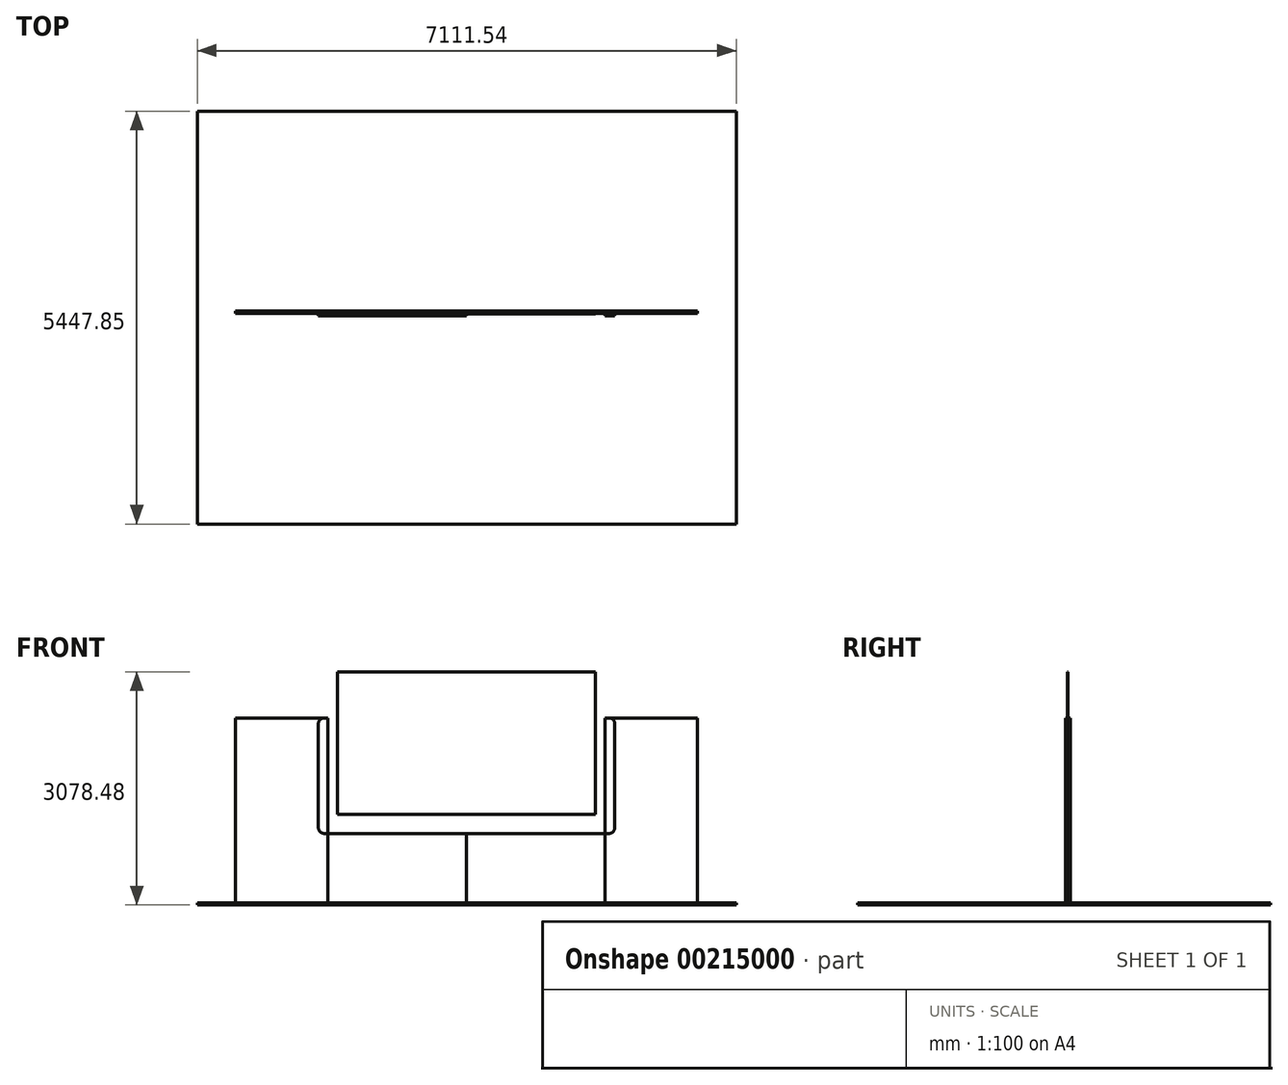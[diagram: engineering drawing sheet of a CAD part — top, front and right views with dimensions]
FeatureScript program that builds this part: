
annotation { "Feature Type Name" : "Feature", "Feature Type Description" : "" }
export const myFeature = defineFeature(function(context is Context, id is Id, definition is map)
    precondition{}
    {
        {
            var Q0;
            Q0=qCreatedBy(makeId("Front.planeOp"),FACE);
            var sketch = newSketch(context, id + "F0", { "sketchPlane" : qUnion([Q0])});
            skLineSegment(sketch, "E0.bottom", {"start": v(0, 0) * mm, "end": v(1219.2, 0) * mm});
            skLineSegment(sketch, "E0.top", {"start": v(0, 2438.4) * mm, "end": v(1219.2, 2438.4) * mm});
            skLineSegment(sketch, "E0.left", {"start": v(0, 0) * mm, "end": v(0, 2438.4) * mm});
            skLineSegment(sketch, "E0.right", {"start": v(1219.2, 0) * mm, "end": v(1219.2, 2438.4) * mm});
            skLineSegment(sketch, "E1.bottom", {"start": v(1219.2, 0) * mm, "end": v(2438.4, 0) * mm});
            skLineSegment(sketch, "E1.top", {"start": v(1219.2, 2438.4) * mm, "end": v(2438.4, 2438.4) * mm});
            skLineSegment(sketch, "E1.right", {"start": v(2438.4, 0) * mm, "end": v(2438.4, 2438.4) * mm});
            skLineSegment(sketch, "E2.bottom", {"start": v(2438.4, 0) * mm, "end": v(4267.2, 0) * mm});
            skLineSegment(sketch, "E2.top", {"start": v(2438.4, 914.4) * mm, "end": v(4267.2, 914.4) * mm});
            skLineSegment(sketch, "E2.left", {"start": v(2438.4, 0) * mm, "end": v(2438.4, 914.4) * mm});
            skLineSegment(sketch, "E2.right", {"start": v(4267.2, 0) * mm, "end": v(4267.2, 914.4) * mm});
            skLineSegment(sketch, "E3.bottom", {"start": v(4267.2, 0) * mm, "end": v(6096, 0) * mm});
            skLineSegment(sketch, "E3.top", {"start": v(4267.2, 914.4) * mm, "end": v(6096, 914.4) * mm});
            skLineSegment(sketch, "E3.right", {"start": v(6096, 0) * mm, "end": v(6096, 914.4) * mm});
            skLineSegment(sketch, "E4.bottom", {"start": v(6096, 0) * mm, "end": v(7315.2, 0) * mm});
            skLineSegment(sketch, "E4.top", {"start": v(6096, 2438.4) * mm, "end": v(7315.2, 2438.4) * mm});
            skLineSegment(sketch, "E4.left", {"start": v(6096, 0) * mm, "end": v(6096, 2438.4) * mm});
            skLineSegment(sketch, "E4.right", {"start": v(7315.2, 0) * mm, "end": v(7315.2, 2438.4) * mm});
            skLineSegment(sketch, "E5.bottom", {"start": v(7315.2, 0) * mm, "end": v(8534.4, 0) * mm});
            skLineSegment(sketch, "E5.top", {"start": v(7315.2, 2438.4) * mm, "end": v(8534.4, 2438.4) * mm});
            skLineSegment(sketch, "E5.right", {"start": v(8534.4, 0) * mm, "end": v(8534.4, 2438.4) * mm});
            skLineSegment(sketch, "E6.bottom", {"start": v(2311.4, 914.4) * mm, "end": v(6223, 914.4) * mm});
            skLineSegment(sketch, "E6.top", {"start": v(2311.4, 3302) * mm, "end": v(6223, 3302) * mm});
            skLineSegment(sketch, "E6.left", {"start": v(2311.4, 914.4) * mm, "end": v(2311.4, 3302) * mm});
            skLineSegment(sketch, "E6.right", {"start": v(6223, 914.4) * mm, "end": v(6223, 3302) * mm});
            skPoint(sketch, "E6.middle", {"position": v(4267.2, 2108.2) * mm});
            skLineSegment(sketch, "E7.0", {"start": v(2565.4, 3048) * mm, "end": v(5969, 3048) * mm});
            skLineSegment(sketch, "E7.1", {"start": v(2565.4, 1168.4) * mm, "end": v(2565.4, 3048) * mm});
            skLineSegment(sketch, "E7.2", {"start": v(2565.4, 1168.4) * mm, "end": v(5969, 1168.4) * mm});
            skLineSegment(sketch, "E7.3", {"start": v(5969, 1168.4) * mm, "end": v(5969, 3048) * mm});
            skLineSegment(sketch, "E8", {"start": v(4267.2, 3048) * mm, "end": v(4267.2, 3302) * mm, "construction": true});
            skLineSegment(sketch, "E9", {"start": v(4267.2, 1168.4) * mm, "end": v(4267.2, 914.4) * mm, "construction": true});
            skLineSegment(sketch, "E10", {"start": v(5969, 2108.2) * mm, "end": v(6223, 2108.2) * mm, "construction": true});
            skLineSegment(sketch, "E11", {"start": v(2565.4, 2108.2) * mm, "end": v(2311.4, 2108.2) * mm, "construction": true});
            skPoint(sketch, "E12", {"position": v(4267.2, 3175) * mm});
            skPoint(sketch, "E13", {"position": v(4267.2, 1041.4) * mm});
            skPoint(sketch, "E14", {"position": v(2438.4, 2108.2) * mm});
            skPoint(sketch, "E15", {"position": v(6096, 2108.2) * mm});
            skLineSegment(sketch, "E16", {"start": v(2438.4, 2108.2) * mm, "end": v(2438.4, 914.4) * mm, "construction": true});
            skSolve(sketch);
        }
        {
            var Q0;
            Q0=makeQuery(id+"F0.imprint","IMPRINT",FACE,{"disambiguationData":[TD([[makeQuery(id+"F0.imprint","IMPRINT",EDGE,{"derivedFrom":sQuery(id+"F0.wireOp",EDGE,"E0.bottom")}),1.0]])]});
            var Q1;
            Q1=makeQuery(id+"F0.imprint","IMPRINT",FACE,{"disambiguationData":[TD([[makeQuery(id+"F0.imprint","IMPRINT",EDGE,{"derivedFrom":sQuery(id+"F0.wireOp",EDGE,"E2.bottom")}),1.0]])]});
            var Q2;
            {var subQ2=sQuery(id+"F0.wireOp",EDGE,"E4.bottom");Q2=makeQuery(id+"F0.imprint","IMPRINT",FACE,{"disambiguationData":[TD([[makeQuery(id+"F0.imprint","IMPRINT",EDGE,{"derivedFrom":subQ2}),1.0]])]});}
            var Q3;
            {var subQ0=sQuery(id+"F0.wireOp",EDGE,"E4.left");var subQ1=sQuery(id+"F0.wireOp",EDGE,"E4.top");var subQ2=makeQuery(id+"F0.imprint","INTERSECT",VERTEX,{"derivedFrom":[subQ1,subQ0]});Q3=makeQuery(id+"F0.imprint","IMPRINT",FACE,{"disambiguationData":[TD([[makeQuery(id+"F0.imprint","IMPRINT",EDGE,{"disambiguationData":[TD([[subQ2,-1.0]])],"derivedFrom":subQ1}),-1.0]])]});}
            extrude(context, id + "F1", {"entities" : qUnion([Q0, Q1, Q2, Q3]), "oppositeDirection" : true, "depth" : 30.48 * mm});
        }
        {
            var Q0;
            Q0=makeQuery(id+"F0.imprint","IMPRINT",FACE,{"disambiguationData":[TD([[makeQuery(id+"F0.imprint","IMPRINT",EDGE,{"derivedFrom":sQuery(id+"F0.wireOp",EDGE,"E1.bottom")}),1.0]])]});
            var Q1;
            {var subQ0=sQuery(id+"F0.wireOp",EDGE,"E1.right");Q1=makeQuery(id+"F0.imprint","IMPRINT",FACE,{"disambiguationData":[TD([[makeQuery(id+"F0.imprint","IMPRINT",EDGE,{"derivedFrom":subQ0}),1.0]])]});}
            var Q2;
            {var subQ0=sQuery(id+"F0.wireOp",EDGE,"E3.bottom");Q2=makeQuery(id+"F0.imprint","IMPRINT",FACE,{"disambiguationData":[TD([[makeQuery(id+"F0.imprint","IMPRINT",EDGE,{"derivedFrom":subQ0}),1.0]])]});}
            var Q3;
            Q3=makeQuery(id+"F0.imprint","IMPRINT",FACE,{"disambiguationData":[TD([[makeQuery(id+"F0.imprint","IMPRINT",EDGE,{"derivedFrom":sQuery(id+"F0.wireOp",EDGE,"E5.bottom")}),1.0]])]});
            extrude(context, id + "F2", {"entities" : qUnion([Q0, Q1, Q2, Q3]), "oppositeDirection" : true, "depth" : 30.48 * mm});
        }
        {
            var Q0;
            {var subQ11=sQuery(id+"F0.wireOp",EDGE,"E1.right");Q0=makeQuery(id+"F0.imprint","IMPRINT",FACE,{"disambiguationData":[TD([[makeQuery(id+"F0.imprint","IMPRINT",EDGE,{"derivedFrom":subQ11}),-1.0]])]});}
            var Q1;
            {var subQ0=sQuery(id+"F0.wireOp",EDGE,"E1.right");Q1=makeQuery(id+"F0.imprint","IMPRINT",FACE,{"disambiguationData":[TD([[makeQuery(id+"F0.imprint","IMPRINT",EDGE,{"derivedFrom":subQ0}),1.0]])]});}
            var Q2;
            {var subQ0=sQuery(id+"F0.wireOp",EDGE,"E4.left");var subQ1=sQuery(id+"F0.wireOp",EDGE,"E4.top");var subQ2=makeQuery(id+"F0.imprint","INTERSECT",VERTEX,{"derivedFrom":[subQ1,subQ0]});Q2=makeQuery(id+"F0.imprint","IMPRINT",FACE,{"disambiguationData":[TD([[makeQuery(id+"F0.imprint","IMPRINT",EDGE,{"disambiguationData":[TD([[subQ2,-1.0]])],"derivedFrom":subQ1}),-1.0]])]});}
            extrude(context, id + "F3", {"entities" : qUnion([Q0, Q1, Q2]), "depth" : 30.48 * mm});
        }
        {
            var Q0;
            Q0=makeQuery(id+"F0.imprint","IMPRINT",FACE,{"disambiguationData":[TD([[makeQuery(id+"F0.imprint","IMPRINT",EDGE,{"derivedFrom":sQuery(id+"F0.wireOp",EDGE,"E7.0")}),-1.0]])]});
            extrude(context, id + "F4", {"entities" : qUnion([Q0]), "depth" : 3.05 * mm});
        }
        {
            var Q0;
            Q0=makeQuery(id+"F3.opExtrude","SWEPT_EDGE",EDGE,{"disambiguationData":[OSD([sQuery(id+"F0.wireOp",EDGE,"E6.top"),sQuery(id+"F0.wireOp",EDGE,"E6.left")])]});
            var Q1;
            Q1=makeQuery(id+"F3.opExtrude","SWEPT_EDGE",EDGE,{"disambiguationData":[OSD([sQuery(id+"F0.wireOp",EDGE,"E7.0"),sQuery(id+"F0.wireOp",EDGE,"E7.1")])]});
            var Q2;
            Q2=makeQuery(id+"F3.opExtrude","SWEPT_EDGE",EDGE,{"disambiguationData":[OSD([sQuery(id+"F0.wireOp",EDGE,"E6.bottom"),sQuery(id+"F0.wireOp",EDGE,"E6.left")])]});
            var Q3;
            Q3=makeQuery(id+"F3.opExtrude","SWEPT_EDGE",EDGE,{"disambiguationData":[OSD([sQuery(id+"F0.wireOp",EDGE,"E7.1"),sQuery(id+"F0.wireOp",EDGE,"E7.2")])]});
            var Q4;
            Q4=makeQuery(id+"F3.opExtrude","SWEPT_EDGE",EDGE,{"disambiguationData":[OSD([sQuery(id+"F0.wireOp",EDGE,"E6.bottom"),sQuery(id+"F0.wireOp",EDGE,"E6.right")])]});
            var Q5;
            Q5=makeQuery(id+"F3.opExtrude","SWEPT_EDGE",EDGE,{"disambiguationData":[OSD([sQuery(id+"F0.wireOp",EDGE,"E7.2"),sQuery(id+"F0.wireOp",EDGE,"E7.3")])]});
            var Q6;
            Q6=makeQuery(id+"F3.opExtrude","SWEPT_EDGE",EDGE,{"disambiguationData":[OSD([sQuery(id+"F0.wireOp",EDGE,"E6.top"),sQuery(id+"F0.wireOp",EDGE,"E6.right")])]});
            var Q7;
            Q7=makeQuery(id+"F3.opExtrude","SWEPT_EDGE",EDGE,{"disambiguationData":[OSD([sQuery(id+"F0.wireOp",EDGE,"E7.0"),sQuery(id+"F0.wireOp",EDGE,"E7.3")])]});
            fillet(context, id + "F5", {"entities" : qUnion([Q0, Q1, Q2, Q3, Q4, Q5, Q6, Q7]), "radius" : 76.2 * mm, "tangentPropagation" : true, "allowEdgeOverflow" : false});
        }
        {
            var Q0;
            Q0=qCreatedBy(makeId("Top.planeOp"),FACE);
            var sketch = newSketch(context, id + "F6", { "sketchPlane" : qUnion([Q0])});
            skLineSegment(sketch, "E17.bottom", {"start": v(714.28, -2776.95) * mm, "end": v(7825.82, -2776.95) * mm});
            skLineSegment(sketch, "E17.top", {"start": v(714.28, 2670.9) * mm, "end": v(7825.82, 2670.9) * mm});
            skLineSegment(sketch, "E17.left", {"start": v(714.28, -2776.95) * mm, "end": v(714.28, 2670.9) * mm});
            skLineSegment(sketch, "E17.right", {"start": v(7825.82, -2776.95) * mm, "end": v(7825.82, 2670.9) * mm});
            skSolve(sketch);
        }
        {
            var Q0;
            Q0=makeQuery(id+"F6.imprint","IMPRINT",FACE,{"disambiguationData":[TD([[makeQuery(id+"F6.imprint","IMPRINT",EDGE,{"derivedFrom":sQuery(id+"F6.wireOp",EDGE,"E17.bottom")}),1.0]])]});
            var Q1;
            Q1=sQuery(id+"F6.wireOp",EDGE,"E17.bottom");
            extrude(context, id + "F7", {"entities" : qUnion([Q0]), "surfaceEntities" : qUnion([Q1]), "oppositeDirection" : true, "depth" : 30.48 * mm});
        }
        {
            var Q0;
            Q0=makeQuery(id+"F2.opExtrude","SWEPT_BODY",BODY,{"disambiguationData":[OSD([sQuery(id+"F0.wireOp",EDGE,"E5.bottom"),sQuery(id+"F0.wireOp",EDGE,"E5.top"),sQuery(id+"F0.wireOp",EDGE,"E4.right"),sQuery(id+"F0.wireOp",EDGE,"E5.right")])]});
            deleteBodies(context, id + "F8", {"entities" : qUnion([Q0])});
        }
        {
            var Q0;
            Q0=makeQuery(id+"F1.opExtrude","SWEPT_BODY",BODY,{"disambiguationData":[OSD([sQuery(id+"F0.wireOp",EDGE,"E0.bottom"),sQuery(id+"F0.wireOp",EDGE,"E0.top"),sQuery(id+"F0.wireOp",EDGE,"E0.left"),sQuery(id+"F0.wireOp",EDGE,"E0.right")])]});
            deleteBodies(context, id + "F9", {"entities" : qUnion([Q0])});
        }
    });
